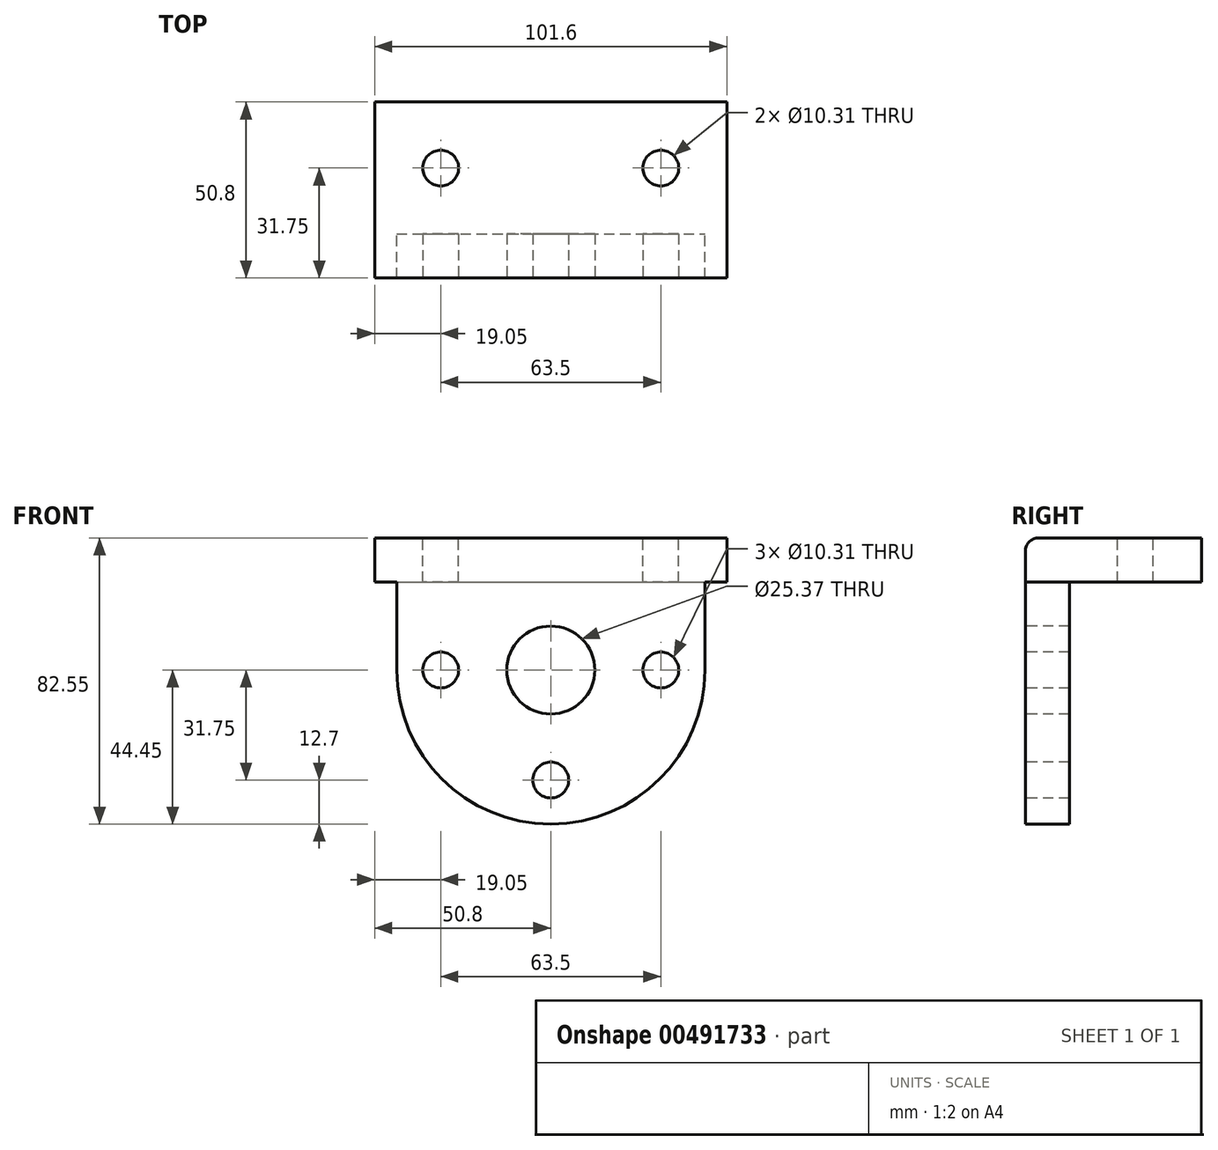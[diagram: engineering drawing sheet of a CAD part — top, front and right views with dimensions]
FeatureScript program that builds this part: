
annotation { "Feature Type Name" : "Feature", "Feature Type Description" : "" }
export const myFeature = defineFeature(function(context is Context, id is Id, definition is map)
    precondition{}
    {
        {
            var Q0;
            Q0=qCreatedBy(makeId("Front.planeOp"),FACE);
            var sketch = newSketch(context, id + "F0", { "sketchPlane" : qUnion([Q0])});
            skArc(sketch, "E0", {"start": v(-44.45, 0) * mm, "mid": v(0, -44.45) * mm, "end": v(44.45, 0) * mm});
            skLineSegment(sketch, "E1.top", {"start": v(-44.45, 25.4) * mm, "end": v(44.45, 25.4) * mm});
            skLineSegment(sketch, "E1.left", {"start": v(-44.45, 0) * mm, "end": v(-44.45, 25.4) * mm});
            skLineSegment(sketch, "E1.right", {"start": v(44.45, 0) * mm, "end": v(44.45, 25.4) * mm});
            skSolve(sketch);
        }
        {
            var Q0;
            Q0 = qSketchRegion(id + "F0", true);
            extrude(context, id + "F1", {"entities" : qUnion([Q0]), "depth" : 12.7 * mm});
        }
        {
            var Q0;
            Q0=makeQuery(id+"F1.opExtrude","SWEPT_FACE",FACE,{"disambiguationData":[OSD([sQuery(id+"F0.wireOp",EDGE,"E1.top")])]});
            var sketch = newSketch(context, id + "F2", { "sketchPlane" : qUnion([Q0])});
            skLineSegment(sketch, "E2.bottom", {"start": v(-50.8, -12.7) * mm, "end": v(50.8, -12.7) * mm});
            skLineSegment(sketch, "E2.top", {"start": v(-50.8, 38.1) * mm, "end": v(50.8, 38.1) * mm});
            skLineSegment(sketch, "E2.left", {"start": v(-50.8, -12.7) * mm, "end": v(-50.8, 38.1) * mm});
            skLineSegment(sketch, "E2.right", {"start": v(50.8, -12.7) * mm, "end": v(50.8, 38.1) * mm});
            skSolve(sketch);
        }
        {
            var Q0;
            Q0 = qSketchRegion(id + "F2", true);
            extrude(context, id + "F3", {"entities" : qUnion([Q0]), "operationType" : NewBodyOperationType.ADD, "depth" : 12.7 * mm});
        }
        {
            var Q0;
            Q0=makeQuery(id+"F3.boolean.opBoolean","MERGE",FACE,{"derivedFrom":[makeQuery(id+"F1.opExtrude","CAP_FACE",FACE,{"disambiguationData":[OSD([sQuery(id+"F0.wireOp",EDGE,"E0"),sQuery(id+"F0.wireOp",EDGE,"E1.top"),sQuery(id+"F0.wireOp",EDGE,"E1.left"),sQuery(id+"F0.wireOp",EDGE,"E1.right")])],"isStart":false}),makeQuery(id+"F3.opExtrude","SWEPT_FACE",FACE,{"disambiguationData":[OSD([sQuery(id+"F2.wireOp",EDGE,"E2.bottom")])]})]});
            var sketch = newSketch(context, id + "F4", { "sketchPlane" : qUnion([Q0])});
            skCircle(sketch, "E3", {"center": v(0, 0) * mm, "radius": 12.68 * mm});
            skSolve(sketch);
        }
        {
            var Q0;
            Q0 = qSketchRegion(id + "F4", true);
            extrude(context, id + "F5", {"entities" : qUnion([Q0]), "operationType" : NewBodyOperationType.REMOVE, "oppositeDirection" : true, "depth" : 25.4 * mm});
        }
        {
            var Q0;
            Q0=makeQuery(id+"F3.boolean.opBoolean","MERGE",FACE,{"derivedFrom":[makeQuery(id+"F1.opExtrude","CAP_FACE",FACE,{"disambiguationData":[OSD([sQuery(id+"F0.wireOp",EDGE,"E0"),sQuery(id+"F0.wireOp",EDGE,"E1.top"),sQuery(id+"F0.wireOp",EDGE,"E1.left"),sQuery(id+"F0.wireOp",EDGE,"E1.right")])],"isStart":false}),makeQuery(id+"F3.opExtrude","SWEPT_FACE",FACE,{"disambiguationData":[OSD([sQuery(id+"F2.wireOp",EDGE,"E2.bottom")])]})]});
            var sketch = newSketch(context, id + "F6", { "sketchPlane" : qUnion([Q0])});
            skCircle(sketch, "E4", {"center": v(0, -31.75) * mm, "radius": 5.16 * mm});
            skCircle(sketch, "E5", {"center": v(-31.75, 0) * mm, "radius": 5.16 * mm});
            skCircle(sketch, "E6", {"center": v(31.75, 0) * mm, "radius": 5.16 * mm});
            skSolve(sketch);
        }
        {
            var Q0;
            Q0 = qSketchRegion(id + "F6", true);
            extrude(context, id + "F7", {"entities" : qUnion([Q0]), "operationType" : NewBodyOperationType.REMOVE, "oppositeDirection" : true, "depth" : 25.4 * mm});
        }
        {
            var Q0;
            Q0=makeQuery(id+"F3.opExtrude","CAP_FACE",FACE,{"disambiguationData":[OSD([sQuery(id+"F2.wireOp",EDGE,"E2.bottom"),sQuery(id+"F2.wireOp",EDGE,"E2.top"),sQuery(id+"F2.wireOp",EDGE,"E2.left"),sQuery(id+"F2.wireOp",EDGE,"E2.right")])],"isStart":false});
            var sketch = newSketch(context, id + "F8", { "sketchPlane" : qUnion([Q0])});
            skCircle(sketch, "E7", {"center": v(-31.75, 19.05) * mm, "radius": 5.16 * mm});
            skCircle(sketch, "E8", {"center": v(31.75, 19.05) * mm, "radius": 5.16 * mm});
            skSolve(sketch);
        }
        {
            var Q0;
            Q0 = qSketchRegion(id + "F8", true);
            extrude(context, id + "F9", {"entities" : qUnion([Q0]), "operationType" : NewBodyOperationType.REMOVE, "oppositeDirection" : true, "depth" : 25.4 * mm});
        }
        {
            var Q0;
            Q0=makeQuery(id+"F1.opExtrude","CAP_EDGE",EDGE,{"disambiguationData":[OSD([sQuery(id+"F0.wireOp",EDGE,"E1.top")])],"isStart":true});
            var Q1;
            Q1=makeQuery(id+"F3.opExtrude","CAP_EDGE",EDGE,{"disambiguationData":[OSD([sQuery(id+"F2.wireOp",EDGE,"E2.bottom")])],"isStart":false});
            fillet(context, id + "F10", {"entities" : qUnion([Q0, Q1]), "radius" : 3.8 * mm, "tangentPropagation" : true, "allowEdgeOverflow" : false});
        }
    });
